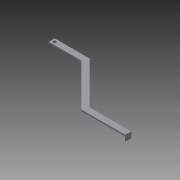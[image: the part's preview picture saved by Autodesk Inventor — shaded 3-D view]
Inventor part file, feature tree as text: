
AUTODESK INVENTOR PART (.ipt)
format: ipt  version: 2013 (Build 170138000, 138)  size: 96,256 bytes
history: native  units: in
note: dims shown in document units (in); Inventor stores cm internally (conversion verified against a paired STEP export)
features: extrude x2, sketch x2
ambient origin geometry x8: Origin, YZ Plane, XZ Plane, XY Plane, X Axis, Y Axis, Z Axis, Center Point
bodies: Solid1 (feature_tree)
feature tree (4):
  extrude  "Extrusion1"  Depth=1.0in
  extrude  "Extrusion2"  Depth=1.0in
  sketch  "Sketch1"  dims[d0=5.5in d1=1.0in]
  sketch  "Sketch2"  dims[d2=112.5deg d3=1.0in d4=135.0deg d5=9.75in d6=0.5in d7=7.0in d8=1.0in d9=0.25in d10=0.0in d11=1.0in d12=1.0in d13=0.0625in d14=0.0in]
